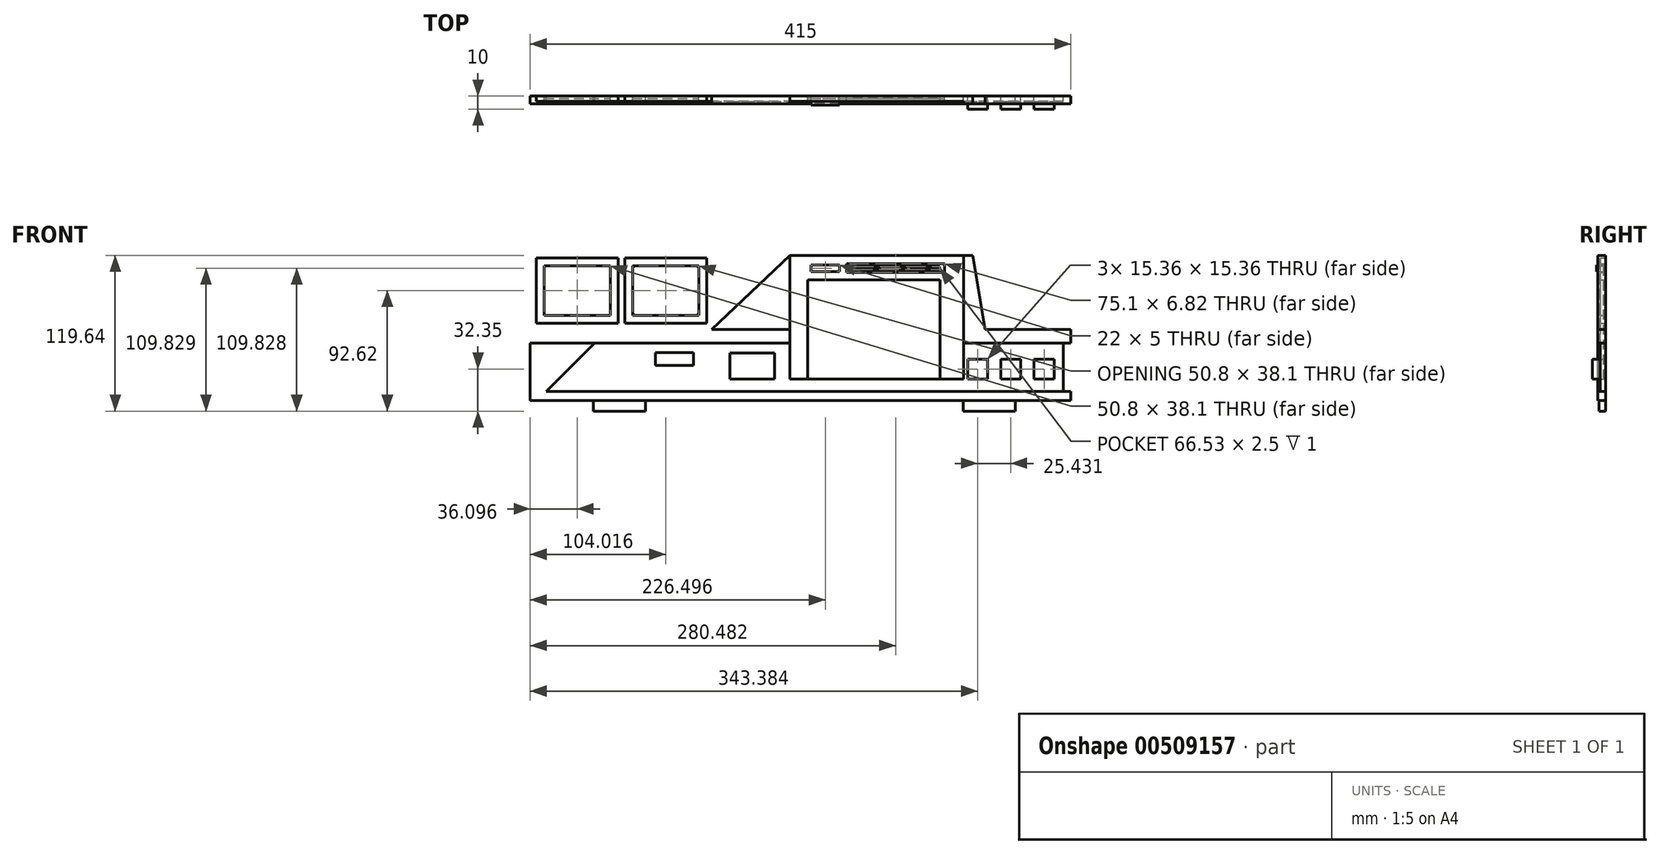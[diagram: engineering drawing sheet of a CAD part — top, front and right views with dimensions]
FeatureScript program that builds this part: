
annotation { "Feature Type Name" : "Feature", "Feature Type Description" : "" }
export const myFeature = defineFeature(function(context is Context, id is Id, definition is map)
    precondition{}
    {
        {
            var Q0;
            Q0=qCreatedBy(makeId("Front.planeOp"),FACE);
            var sketch = newSketch(context, id + "F0", { "sketchPlane" : qUnion([Q0])});
            skLineSegment(sketch, "E0.bottom", {"start": v(-253.03, 48.9) * mm, "end": v(-202.23, 48.9) * mm});
            skLineSegment(sketch, "E0.top", {"start": v(-253.03, 10.8) * mm, "end": v(-202.23, 10.8) * mm});
            skLineSegment(sketch, "E0.left", {"start": v(-253.03, 48.9) * mm, "end": v(-253.03, 10.8) * mm});
            skLineSegment(sketch, "E0.right", {"start": v(-202.23, 48.9) * mm, "end": v(-202.23, 10.8) * mm});
            skLineSegment(sketch, "E1.bottom", {"start": v(-185.11, 48.9) * mm, "end": v(-134.31, 48.9) * mm});
            skLineSegment(sketch, "E1.top", {"start": v(-185.11, 10.8) * mm, "end": v(-134.31, 10.8) * mm});
            skLineSegment(sketch, "E1.left", {"start": v(-185.11, 48.9) * mm, "end": v(-185.11, 10.8) * mm});
            skLineSegment(sketch, "E1.right", {"start": v(-134.31, 48.9) * mm, "end": v(-134.31, 10.8) * mm});
            skLineSegment(sketch, "E2.bottom", {"start": v(-50.8, 38.1) * mm, "end": v(50.8, 38.1) * mm});
            skLineSegment(sketch, "E2.top", {"start": v(-50.8, -38.1) * mm, "end": v(50.8, -38.1) * mm});
            skLineSegment(sketch, "E2.left", {"start": v(-50.8, 38.1) * mm, "end": v(-50.8, -38.1) * mm});
            skLineSegment(sketch, "E2.right", {"start": v(50.8, 38.1) * mm, "end": v(50.8, -38.1) * mm});
            skPoint(sketch, "E2.middle", {"position": v(0, 0) * mm});
            skLineSegment(sketch, "E3.bottom", {"start": v(71.97, -22.74) * mm, "end": v(87.33, -22.74) * mm});
            skLineSegment(sketch, "E3.top", {"start": v(71.97, -38.1) * mm, "end": v(87.33, -38.1) * mm});
            skLineSegment(sketch, "E3.left", {"start": v(71.97, -22.74) * mm, "end": v(71.97, -38.1) * mm});
            skLineSegment(sketch, "E3.right", {"start": v(87.33, -22.74) * mm, "end": v(87.33, -38.1) * mm});
            skLineSegment(sketch, "E4.bottom", {"start": v(97.4, -38.1) * mm, "end": v(112.77, -38.1) * mm});
            skLineSegment(sketch, "E4.top", {"start": v(97.4, -22.74) * mm, "end": v(112.77, -22.74) * mm});
            skLineSegment(sketch, "E4.left", {"start": v(97.4, -38.1) * mm, "end": v(97.4, -22.74) * mm});
            skLineSegment(sketch, "E4.right", {"start": v(112.77, -38.1) * mm, "end": v(112.77, -22.74) * mm});
            skPoint(sketch, "E5.firstSnap0", {"position": v(105.09, -38.1) * mm});
            skLineSegment(sketch, "E5.bottom", {"start": v(123.05, -38.1) * mm, "end": v(138.4, -38.1) * mm});
            skLineSegment(sketch, "E5.top", {"start": v(123.05, -22.74) * mm, "end": v(138.4, -22.74) * mm});
            skLineSegment(sketch, "E5.left", {"start": v(123.05, -38.1) * mm, "end": v(123.05, -22.74) * mm});
            skLineSegment(sketch, "E5.right", {"start": v(138.4, -38.1) * mm, "end": v(138.4, -22.74) * mm});
            skLineSegment(sketch, "E6.bottom", {"start": v(-20.8, 50.47) * mm, "end": v(54.3, 50.47) * mm});
            skLineSegment(sketch, "E6.top", {"start": v(-20.8, 43.65) * mm, "end": v(54.3, 43.65) * mm});
            skLineSegment(sketch, "E6.left", {"start": v(-20.8, 50.47) * mm, "end": v(-20.8, 43.65) * mm});
            skLineSegment(sketch, "E6.right", {"start": v(54.3, 50.47) * mm, "end": v(54.3, 43.65) * mm});
            skLineSegment(sketch, "E7.bottom", {"start": v(-167.47, -17.7) * mm, "end": v(-138.45, -17.7) * mm});
            skLineSegment(sketch, "E7.top", {"start": v(-167.47, -27.69) * mm, "end": v(-138.45, -27.69) * mm});
            skLineSegment(sketch, "E7.left", {"start": v(-167.47, -17.7) * mm, "end": v(-167.47, -27.7) * mm});
            skLineSegment(sketch, "E7.right", {"start": v(-138.45, -17.69) * mm, "end": v(-138.45, -27.69) * mm});
            skLineSegment(sketch, "E8.bottom", {"start": v(-110.33, -18.1) * mm, "end": v(-76.1, -18.1) * mm});
            skLineSegment(sketch, "E8.top", {"start": v(-110.33, -38.1) * mm, "end": v(-76.1, -38.1) * mm});
            skLineSegment(sketch, "E8.left", {"start": v(-110.33, -18.1) * mm, "end": v(-110.33, -38.1) * mm});
            skLineSegment(sketch, "E8.right", {"start": v(-76.1, -18.1) * mm, "end": v(-76.1, -38.1) * mm});
            skLineSegment(sketch, "E9.bottom", {"start": v(151.27, -47.64) * mm, "end": v(-263.73, -47.64) * mm});
            skLineSegment(sketch, "E9.top", {"start": v(151.27, -54.7) * mm, "end": v(-263.73, -54.7) * mm});
            skLineSegment(sketch, "E9.left", {"start": v(151.27, -47.64) * mm, "end": v(151.27, -54.7) * mm});
            skLineSegment(sketch, "E9.right", {"start": v(-263.73, -47.64) * mm, "end": v(-263.73, -54.7) * mm});
            skLineSegment(sketch, "E10.bottom", {"start": v(-48.23, 49.56) * mm, "end": v(-26.23, 49.56) * mm});
            skLineSegment(sketch, "E10.top", {"start": v(-48.23, 44.56) * mm, "end": v(-26.23, 44.56) * mm});
            skLineSegment(sketch, "E10.left", {"start": v(-48.23, 49.56) * mm, "end": v(-48.23, 44.56) * mm});
            skLineSegment(sketch, "E10.right", {"start": v(-26.23, 49.56) * mm, "end": v(-26.23, 44.56) * mm});
            skLineSegment(sketch, "E11.bottom", {"start": v(-64.45, -38.1) * mm, "end": v(68.97, -38.1) * mm});
            skLineSegment(sketch, "E11.top", {"start": v(-64.45, 56.87) * mm, "end": v(68.97, 56.87) * mm});
            skLineSegment(sketch, "E11.left", {"start": v(-64.45, -38.1) * mm, "end": v(-64.45, 56.87) * mm});
            skLineSegment(sketch, "E11.right", {"start": v(68.97, -38.1) * mm, "end": v(68.97, 56.87) * mm});
            skLineSegment(sketch, "E12.bottom", {"start": v(-259.03, 54.9) * mm, "end": v(-196.23, 54.9) * mm});
            skLineSegment(sketch, "E12.top", {"start": v(-259.03, 4.8) * mm, "end": v(-196.23, 4.8) * mm});
            skLineSegment(sketch, "E12.left", {"start": v(-259.03, 54.9) * mm, "end": v(-259.03, 4.8) * mm});
            skLineSegment(sketch, "E12.right", {"start": v(-196.23, 54.9) * mm, "end": v(-196.23, 4.8) * mm});
            skLineSegment(sketch, "E13.bottom", {"start": v(-191.11, 54.9) * mm, "end": v(-128.31, 54.9) * mm});
            skLineSegment(sketch, "E13.top", {"start": v(-191.11, 4.8) * mm, "end": v(-128.31, 4.8) * mm});
            skLineSegment(sketch, "E13.left", {"start": v(-191.11, 54.9) * mm, "end": v(-191.11, 4.8) * mm});
            skLineSegment(sketch, "E13.right", {"start": v(-128.31, 54.9) * mm, "end": v(-128.31, 4.8) * mm});
            skPoint(sketch, "E14.oppositeSnap0", {"position": v(-50.8, 0) * mm});
            skLineSegment(sketch, "E14.bottom", {"start": v(-263.73, -47.64) * mm, "end": v(-64.45, -47.64) * mm});
            skLineSegment(sketch, "E14.top", {"start": v(-263.73, 0) * mm, "end": v(-64.45, 0) * mm});
            skLineSegment(sketch, "E14.left", {"start": v(-263.73, -47.64) * mm, "end": v(-263.73, 0) * mm});
            skLineSegment(sketch, "E14.right", {"start": v(-64.45, -47.64) * mm, "end": v(-64.45, 0) * mm});
            skLineSegment(sketch, "E15.top", {"start": v(-263.73, -10.6) * mm, "end": v(-64.45, -10.59) * mm});
            skLineSegment(sketch, "E15.left", {"start": v(-263.73, 0) * mm, "end": v(-263.73, -10.6) * mm});
            skLineSegment(sketch, "E15.right", {"start": v(-64.45, 0) * mm, "end": v(-64.45, -10.59) * mm});
            skPoint(sketch, "E16", {"position": v(-251.38, -47.64) * mm});
            skPoint(sketch, "E17", {"position": v(-214.33, -10.6) * mm});
            skLineSegment(sketch, "E18", {"start": v(-251.38, -47.64) * mm, "end": v(-214.33, -10.6) * mm});
            skPoint(sketch, "E19", {"position": v(-124.45, 0) * mm});
            skLineSegment(sketch, "E20", {"start": v(-64.45, 56.87) * mm, "end": v(-124.45, 0) * mm});
            skPoint(sketch, "E21.firstSnap0", {"position": v(50.8, 0) * mm});
            skLineSegment(sketch, "E21.bottom", {"start": v(68.97, 0) * mm, "end": v(151.27, 0) * mm});
            skLineSegment(sketch, "E21.top", {"start": v(68.97, -10.59) * mm, "end": v(151.27, -10.59) * mm});
            skLineSegment(sketch, "E21.left", {"start": v(68.97, 0) * mm, "end": v(68.97, -10.59) * mm});
            skLineSegment(sketch, "E21.right", {"start": v(151.27, 0) * mm, "end": v(151.27, -10.59) * mm});
            skLineSegment(sketch, "E22.bottom", {"start": v(145.34, -10.59) * mm, "end": v(68.97, -10.59) * mm});
            skLineSegment(sketch, "E22.top", {"start": v(145.34, -47.64) * mm, "end": v(68.97, -47.64) * mm});
            skLineSegment(sketch, "E22.left", {"start": v(145.34, -10.59) * mm, "end": v(145.34, -47.64) * mm});
            skLineSegment(sketch, "E22.right", {"start": v(68.97, -10.59) * mm, "end": v(68.97, -47.64) * mm});
            skLineSegment(sketch, "E23", {"start": v(68.97, 56.87) * mm, "end": v(75.9, 56.87) * mm});
            skLineSegment(sketch, "E24", {"start": v(75.9, 56.87) * mm, "end": v(85.49, 0) * mm});
            skSolve(sketch);
        }
        {
            var Q0;
            Q0=makeQuery(id+"F0.imprint","IMPRINT",FACE,{"disambiguationData":[TD([[makeQuery(id+"F0.imprint","IMPRINT",EDGE,{"derivedFrom":sQuery(id+"F0.wireOp",EDGE,"E5.bottom")}),1.0]])]});
            var Q1;
            Q1=makeQuery(id+"F0.imprint","IMPRINT",FACE,{"disambiguationData":[TD([[makeQuery(id+"F0.imprint","IMPRINT",EDGE,{"derivedFrom":sQuery(id+"F0.wireOp",EDGE,"E4.bottom")}),1.0]])]});
            var Q2;
            Q2=makeQuery(id+"F0.imprint","IMPRINT",FACE,{"disambiguationData":[TD([[makeQuery(id+"F0.imprint","IMPRINT",EDGE,{"derivedFrom":sQuery(id+"F0.wireOp",EDGE,"E3.bottom")}),-1.0]])]});
            extrude(context, id + "F1", {"entities" : qUnion([Q0, Q1, Q2]), "depth" : 10 * mm, "offsetDistance" : 25 * mm});
        }
        {
            var Q0;
            Q0=makeQuery(id+"F0.imprint","IMPRINT",FACE,{"disambiguationData":[TD([[makeQuery(id+"F0.imprint","IMPRINT",EDGE,{"derivedFrom":sQuery(id+"F0.wireOp",EDGE,"E0.bottom")}),-1.0]])]});
            var Q1;
            Q1=makeQuery(id+"F0.imprint","IMPRINT",FACE,{"disambiguationData":[TD([[makeQuery(id+"F0.imprint","IMPRINT",EDGE,{"derivedFrom":sQuery(id+"F0.wireOp",EDGE,"E1.bottom")}),-1.0]])]});
            var Q2;
            Q2=makeQuery(id+"F0.imprint","IMPRINT",FACE,{"disambiguationData":[TD([[makeQuery(id+"F0.imprint","IMPRINT",EDGE,{"derivedFrom":sQuery(id+"F0.wireOp",EDGE,"E2.bottom")}),-1.0]])]});
            var Q3;
            Q3=makeQuery(id+"F0.imprint","IMPRINT",FACE,{"disambiguationData":[TD([[makeQuery(id+"F0.imprint","IMPRINT",EDGE,{"derivedFrom":sQuery(id+"F0.wireOp",EDGE,"E6.bottom")}),-1.0]])]});
            var Q4;
            Q4=makeQuery(id+"F0.imprint","IMPRINT",FACE,{"disambiguationData":[TD([[makeQuery(id+"F0.imprint","IMPRINT",EDGE,{"derivedFrom":sQuery(id+"F0.wireOp",EDGE,"E10.bottom")}),-1.0]])]});
            extrude(context, id + "F2", {"entities" : qUnion([Q0, Q1, Q2, Q3, Q4]), "depth" : 2 * mm, "offsetDistance" : 25 * mm});
        }
        {
            var Q0;
            Q0=makeQuery(id+"F2.opExtrude","CAP_FACE",FACE,{"disambiguationData":[OSD([sQuery(id+"F0.wireOp",EDGE,"E6.bottom"),sQuery(id+"F0.wireOp",EDGE,"E6.top"),sQuery(id+"F0.wireOp",EDGE,"E6.left"),sQuery(id+"F0.wireOp",EDGE,"E6.right")])],"isStart":false});
            var sketch = newSketch(context, id + "F3", { "sketchPlane" : qUnion([Q0])});
            skLineSegment(sketch, "E25.bottom", {"start": v(-15.97, 48.39) * mm, "end": v(50.56, 48.39) * mm});
            skLineSegment(sketch, "E25.top", {"start": v(-15.97, 45.89) * mm, "end": v(50.56, 45.89) * mm});
            skLineSegment(sketch, "E25.left", {"start": v(-15.97, 48.39) * mm, "end": v(-15.97, 45.89) * mm});
            skLineSegment(sketch, "E25.right", {"start": v(50.56, 48.39) * mm, "end": v(50.56, 45.89) * mm});
            skSolve(sketch);
        }
        {
            var Q0;
            Q0 = qSketchRegion(id + "F3", true);
            extrude(context, id + "F4", {"entities" : qUnion([Q0]), "operationType" : NewBodyOperationType.REMOVE, "oppositeDirection" : true, "depth" : 1 * mm, "offsetDistance" : 25 * mm});
        }
        {
            var Q0;
            Q0=makeQuery(id+"F0.imprint","IMPRINT",FACE,{"disambiguationData":[TD([[makeQuery(id+"F0.imprint","IMPRINT",EDGE,{"derivedFrom":sQuery(id+"F0.wireOp",EDGE,"E2.bottom")}),1.0]])]});
            extrude(context, id + "F5", {"entities" : qUnion([Q0]), "depth" : 4 * mm, "offsetDistance" : 25 * mm});
        }
        {
            var Q0;
            Q0=makeQuery(id+"F2.opExtrude","CAP_FACE",FACE,{"disambiguationData":[OSD([sQuery(id+"F0.wireOp",EDGE,"E10.bottom"),sQuery(id+"F0.wireOp",EDGE,"E10.top"),sQuery(id+"F0.wireOp",EDGE,"E10.left"),sQuery(id+"F0.wireOp",EDGE,"E10.right")])],"isStart":false});
            extrude(context, id + "F6", {"entities" : qUnion([Q0]), "depth" : 5 * mm, "offsetDistance" : 25 * mm});
        }
        {
            var Q0;
            Q0=makeQuery(id+"F0.imprint","IMPRINT",FACE,{"disambiguationData":[TD([[makeQuery(id+"F0.imprint","IMPRINT",EDGE,{"derivedFrom":sQuery(id+"F0.wireOp",EDGE,"E0.bottom")}),1.0]])]});
            var Q1;
            Q1=makeQuery(id+"F0.imprint","IMPRINT",FACE,{"disambiguationData":[TD([[makeQuery(id+"F0.imprint","IMPRINT",EDGE,{"derivedFrom":sQuery(id+"F0.wireOp",EDGE,"E1.bottom")}),1.0]])]});
            extrude(context, id + "F7", {"entities" : qUnion([Q0, Q1]), "depth" : 4 * mm, "offsetDistance" : 25 * mm});
        }
        {
            var Q0;
            Q0=makeQuery(id+"F7.opExtrude","SWEPT_EDGE",EDGE,{"disambiguationData":[OSD([sQuery(id+"F0.wireOp",EDGE,"E1.bottom"),sQuery(id+"F0.wireOp",EDGE,"E1.right")])]});
            var Q1;
            Q1=makeQuery(id+"F7.opExtrude","SWEPT_EDGE",EDGE,{"disambiguationData":[OSD([sQuery(id+"F0.wireOp",EDGE,"E1.bottom"),sQuery(id+"F0.wireOp",EDGE,"E1.left")])]});
            var Q2;
            Q2=makeQuery(id+"F7.opExtrude","SWEPT_EDGE",EDGE,{"disambiguationData":[OSD([sQuery(id+"F0.wireOp",EDGE,"E1.top"),sQuery(id+"F0.wireOp",EDGE,"E1.right")])]});
            var Q3;
            Q3=makeQuery(id+"F7.opExtrude","SWEPT_EDGE",EDGE,{"disambiguationData":[OSD([sQuery(id+"F0.wireOp",EDGE,"E1.top"),sQuery(id+"F0.wireOp",EDGE,"E1.left")])]});
            fillet(context, id + "F8", {"entities" : qUnion([Q0, Q1, Q2, Q3]), "radius" : 2.5 * mm, "tangentPropagation" : true, "allowEdgeOverflow" : false});
        }
        {
            var Q0;
            {var subQ3=sQuery(id+"F0.wireOp",EDGE,"E15.left");Q0=makeQuery(id+"F0.imprint","IMPRINT",FACE,{"disambiguationData":[TD([[makeQuery(id+"F0.imprint","IMPRINT",EDGE,{"derivedFrom":subQ3}),1.0]])]});}
            var Q1;
            {var subQ0=sQuery(id+"F0.wireOp",EDGE,"E14.left");Q1=makeQuery(id+"F0.imprint","IMPRINT",FACE,{"disambiguationData":[TD([[makeQuery(id+"F0.imprint","IMPRINT",EDGE,{"derivedFrom":subQ0}),-1.0]])]});}
            var Q2;
            {var subQ0=sQuery(id+"F0.wireOp",EDGE,"E11.left");Q2=makeQuery(id+"F0.imprint","IMPRINT",FACE,{"disambiguationData":[TD([[makeQuery(id+"F0.imprint","IMPRINT",EDGE,{"derivedFrom":subQ0}),1.0]])]});}
            var Q3;
            {var subQ2=sQuery(id+"F0.wireOp",EDGE,"E9.bottom");Q3=makeQuery(id+"F0.imprint","IMPRINT",FACE,{"disambiguationData":[TD([[makeQuery(id+"F0.imprint","IMPRINT",EDGE,{"derivedFrom":subQ2}),1.0]])]});}
            var Q4;
            {var subQ0=sQuery(id+"F0.wireOp",EDGE,"E11.right");Q4=makeQuery(id+"F0.imprint","IMPRINT",FACE,{"disambiguationData":[TD([[makeQuery(id+"F0.imprint","IMPRINT",EDGE,{"derivedFrom":subQ0}),-1.0]])]});}
            var Q5;
            Q5=makeQuery(id+"F0.imprint","IMPRINT",FACE,{"disambiguationData":[TD([[makeQuery(id+"F0.imprint","IMPRINT",EDGE,{"derivedFrom":sQuery(id+"F0.wireOp",EDGE,"E21.top")}),1.0]])]});
            extrude(context, id + "F9", {"entities" : qUnion([Q0, Q1, Q2, Q3, Q4, Q5]), "operationType" : NewBodyOperationType.ADD, "depth" : 6 * mm, "offsetDistance" : 25 * mm});
        }
        {
            var Q0;
            Q0=makeQuery(id+"F0.imprint","IMPRINT",FACE,{"disambiguationData":[TD([[makeQuery(id+"F0.imprint","IMPRINT",EDGE,{"derivedFrom":sQuery(id+"F0.wireOp",EDGE,"E7.bottom")}),1.0]])]});
            var Q1;
            {var subQ0=sQuery(id+"F0.wireOp",EDGE,"E11.bottom");var subQ1=makeQuery(id+"F0.imprint","INTERSECT",VERTEX,{"derivedFrom":[sQuery(id+"F0.wireOp",EDGE,"E2.left"),subQ0]});Q1=makeQuery(id+"F0.imprint","IMPRINT",FACE,{"disambiguationData":[TD([[makeQuery(id+"F0.imprint","IMPRINT",EDGE,{"disambiguationData":[TD([[subQ1,1.0]])],"derivedFrom":subQ0}),-1.0]])]});}
            var Q2;
            Q2=makeQuery(id+"F0.imprint","IMPRINT",FACE,{"disambiguationData":[TD([[makeQuery(id+"F0.imprint","IMPRINT",EDGE,{"derivedFrom":sQuery(id+"F0.wireOp",EDGE,"E3.bottom")}),1.0]])]});
            extrude(context, id + "F10", {"entities" : qUnion([Q0, Q1, Q2]), "depth" : 4 * mm, "offsetDistance" : 25 * mm});
        }
        {
            var Q0;
            Q0=makeQuery(id+"F0.imprint","IMPRINT",FACE,{"disambiguationData":[TD([[makeQuery(id+"F0.imprint","IMPRINT",EDGE,{"derivedFrom":sQuery(id+"F0.wireOp",EDGE,"E7.bottom")}),-1.0]])]});
            var Q1;
            Q1=makeQuery(id+"F0.imprint","IMPRINT",FACE,{"disambiguationData":[TD([[makeQuery(id+"F0.imprint","IMPRINT",EDGE,{"derivedFrom":sQuery(id+"F0.wireOp",EDGE,"E8.bottom")}),-1.0]])]});
            extrude(context, id + "F11", {"entities" : qUnion([Q0, Q1]), "operationType" : NewBodyOperationType.ADD, "depth" : 6 * mm, "offsetDistance" : 25 * mm});
        }
        {
            var Q0;
            Q0=qCreatedBy(makeId("Front.planeOp"),FACE);
            var sketch = newSketch(context, id + "F12", { "sketchPlane" : qUnion([Q0])});
            skLineSegment(sketch, "E26.bottom", {"start": v(-215.2, -54.77) * mm, "end": v(-175.2, -54.77) * mm});
            skLineSegment(sketch, "E26.top", {"start": v(-215.2, -62.77) * mm, "end": v(-175.2, -62.77) * mm});
            skLineSegment(sketch, "E26.left", {"start": v(-215.2, -54.77) * mm, "end": v(-215.2, -62.77) * mm});
            skLineSegment(sketch, "E26.right", {"start": v(-175.2, -54.77) * mm, "end": v(-175.2, -62.77) * mm});
            skLineSegment(sketch, "E27.bottom", {"start": v(68.47, -54.77) * mm, "end": v(108.47, -54.77) * mm});
            skLineSegment(sketch, "E27.top", {"start": v(68.47, -62.77) * mm, "end": v(108.47, -62.77) * mm});
            skLineSegment(sketch, "E27.left", {"start": v(68.47, -54.77) * mm, "end": v(68.47, -62.77) * mm});
            skLineSegment(sketch, "E27.right", {"start": v(108.47, -54.77) * mm, "end": v(108.47, -62.77) * mm});
            skSolve(sketch);
        }
        {
            var Q0;
            Q0 = qSketchRegion(id + "F12", true);
            extrude(context, id + "F13", {"entities" : qUnion([Q0]), "depth" : 5 * mm, "offsetDistance" : 25 * mm});
        }
    });
